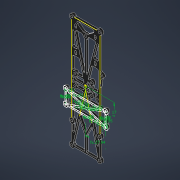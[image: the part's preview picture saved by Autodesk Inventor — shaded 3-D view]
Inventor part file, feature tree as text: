
AUTODESK INVENTOR PART (.ipt)
format: ipt  version: 2021 (Build 250183000, 183)  size: 1,041,920 bytes
history: native  units: mm
features: other x11, reference x8, extrude x5, fillet x2, hole x1, projected_geometry x1
ambient origin geometry x8: Origin, YZ Plane, XZ Plane, XY Plane, X Axis, Y Axis, Z Axis, Center Point
bodies: Body1 (feature_tree)
feature tree (28):
  other  "plate"
  extrude  "pca9685_mount"  Depth=2.0mm
  extrude  "sensor_9dof_mount"  Depth=2.0mm
  extrude  "power_distribution_mount"  Depth=2.0mm
  extrude  "holes_fill"  Depth=2.0mm
  extrude  "bec_ziptie_holes"  Depth=2.0mm
  fillet  "bec_ziptie_reinforcement"  Radius=2.0mm
  fillet  "all"  Radius=7.1mm
  other  "plate_sketch"
  reference  "Reference1"
  reference  "Reference3"
  reference  "Reference4"
  reference  "Reference7"
  reference  "Reference8"
  reference  "Reference9"
  other  "pca9685_mount_sketch"
  other  "adafruit_9dof_mount_sketch"
  reference  "Reference10"
  reference  "Reference11"
  hole  "holes_fill_sketch"  [1 undecoded]
  projected_geometry  "Projected Loop1"
  other  "power_distribution_mount_sketch"
  other  "bec_ziptie_holes_sketch"
  parser-record x1  (decoder bookkeeping rows leaked as tree rows — omitted from the tree; the rows remain in map.json)
  other  "plate_electronics.iam"
  other  "top_short:1"
  other  "standoff_3m20mm:9"
  other  "standoff_3m20mm:10"
note: 1 required parameter value undecoded (feature->parameter linkage not recoverable at this tier; creation-order binding heuristic only, values carry confidence <= 0.55)
note: 1 file-system path scrubbed to <path> (originals preserved in map.json)
